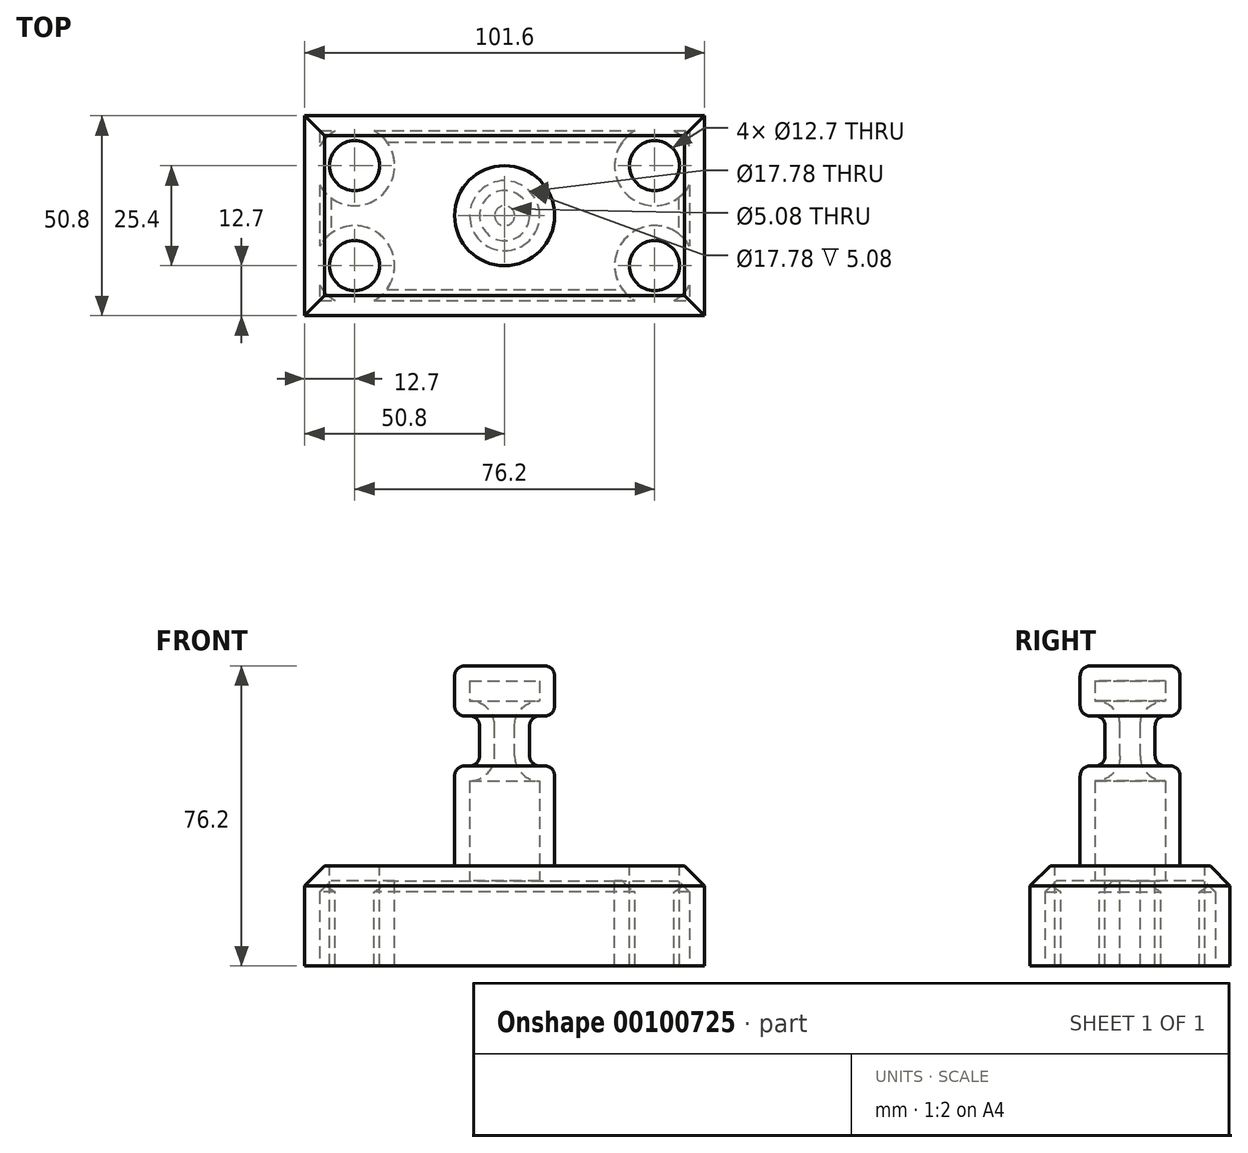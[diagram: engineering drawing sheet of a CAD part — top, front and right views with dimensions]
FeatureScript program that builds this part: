
annotation { "Feature Type Name" : "Feature", "Feature Type Description" : "" }
export const myFeature = defineFeature(function(context is Context, id is Id, definition is map)
    precondition{}
    {
        {
            var Q0;
            Q0=qCreatedBy(makeId("Top.planeOp"),FACE);
            var sketch = newSketch(context, id + "F0", { "sketchPlane" : qUnion([Q0])});
            skLineSegment(sketch, "E0.bottom", {"start": v(-50.8, 25.4) * mm, "end": v(50.8, 25.4) * mm});
            skLineSegment(sketch, "E0.top", {"start": v(-50.8, -25.4) * mm, "end": v(50.8, -25.4) * mm});
            skLineSegment(sketch, "E0.left", {"start": v(-50.8, 25.4) * mm, "end": v(-50.8, -25.4) * mm});
            skLineSegment(sketch, "E0.right", {"start": v(50.8, 25.4) * mm, "end": v(50.8, -25.4) * mm});
            skPoint(sketch, "E0.middle", {"position": v(0, 0) * mm});
            skSolve(sketch);
        }
        {
            var Q0;
            Q0=makeQuery(id+"F0.imprint","IMPRINT",FACE,{"disambiguationData":[TD([[makeQuery(id+"F0.imprint","IMPRINT",EDGE,{"derivedFrom":sQuery(id+"F0.wireOp",EDGE,"E0.bottom")}),-1.0]])]});
            extrude(context, id + "F1", {"entities" : qUnion([Q0]), "depth" : 25.4 * mm});
        }
        {
            var Q0;
            Q0=makeQuery(id+"F1.opExtrude","CAP_FACE",FACE,{"disambiguationData":[OSD([sQuery(id+"F0.wireOp",EDGE,"E0.bottom"),sQuery(id+"F0.wireOp",EDGE,"E0.top"),sQuery(id+"F0.wireOp",EDGE,"E0.left"),sQuery(id+"F0.wireOp",EDGE,"E0.right")])],"isStart":false});
            var sketch = newSketch(context, id + "F2", { "sketchPlane" : qUnion([Q0])});
            skCircle(sketch, "E1", {"center": v(-38.1, 12.7) * mm, "radius": 6.35 * mm});
            skCircle(sketch, "E2", {"center": v(38.1, 12.7) * mm, "radius": 6.35 * mm});
            skCircle(sketch, "E3", {"center": v(38.1, -12.7) * mm, "radius": 6.35 * mm});
            skCircle(sketch, "E4", {"center": v(-38.1, -12.7) * mm, "radius": 6.35 * mm});
            skSolve(sketch);
        }
        {
            var Q0;
            Q0 = qSketchRegion(id + "F2", true);
            extrude(context, id + "F3", {"entities" : qUnion([Q0]), "operationType" : NewBodyOperationType.REMOVE, "endBound" : BoundingType.THROUGH_ALL, "oppositeDirection" : true, "depth" : 25.4 * mm});
        }
        {
            var Q0;
            Q0=qCreatedBy(makeId("Front.planeOp"),FACE);
            var sketch = newSketch(context, id + "F4", { "sketchPlane" : qUnion([Q0])});
            skLineSegment(sketch, "E5.bottom", {"start": v(0, 25.4) * mm, "end": v(-12.7, 25.4) * mm});
            skLineSegment(sketch, "E5.top", {"start": v(0, 76.2) * mm, "end": v(-12.7, 76.2) * mm});
            skLineSegment(sketch, "E5.left", {"start": v(0, 25.4) * mm, "end": v(0, 76.2) * mm});
            skLineSegment(sketch, "E5.right", {"start": v(-12.7, 25.4) * mm, "end": v(-12.7, 76.2) * mm});
            skSolve(sketch);
        }
        {
            var Q0;
            Q0=makeQuery(id+"F4.imprint","IMPRINT",FACE,{"disambiguationData":[TD([[makeQuery(id+"F4.imprint","IMPRINT",EDGE,{"derivedFrom":sQuery(id+"F4.wireOp",EDGE,"E5.bottom")}),-1.0]])]});
            var Q1;
            Q1=sQuery(id+"F4.wireOp",EDGE,"E5.left");
            revolve(context, id + "F5", {"operationType" : NewBodyOperationType.ADD, "entities" : qUnion([Q0]), "axis" : qUnion([Q1]), "revolveType" : RevolveType.FULL});
        }
        {
            var Q0;
            Q0=qCreatedBy(makeId("Front.planeOp"),FACE);
            var sketch = newSketch(context, id + "F6", { "sketchPlane" : qUnion([Q0])});
            skLineSegment(sketch, "E6.bottom", {"start": v(-16.07, 63.5) * mm, "end": v(-6.35, 63.5) * mm});
            skLineSegment(sketch, "E6.top", {"start": v(-16.07, 50.8) * mm, "end": v(-6.35, 50.8) * mm});
            skLineSegment(sketch, "E6.left", {"start": v(-16.07, 63.5) * mm, "end": v(-16.07, 50.8) * mm});
            skLineSegment(sketch, "E6.right", {"start": v(-6.35, 63.5) * mm, "end": v(-6.35, 50.8) * mm});
            skLineSegment(sketch, "E7", {"start": v(0, 0) * mm, "end": v(0, 76.26) * mm, "construction": true});
            skSolve(sketch);
        }
        {
            var Q0;
            Q0=makeQuery(id+"F6.imprint","IMPRINT",FACE,{"disambiguationData":[TD([[makeQuery(id+"F6.imprint","IMPRINT",EDGE,{"derivedFrom":sQuery(id+"F6.wireOp",EDGE,"E6.bottom")}),-1.0]])]});
            var Q1;
            Q1=sQuery(id+"F6.wireOp",EDGE,"E7");
            revolve(context, id + "F7", {"operationType" : NewBodyOperationType.REMOVE, "entities" : qUnion([Q0]), "axis" : qUnion([Q1]), "revolveType" : RevolveType.FULL, "oppositeDirection" : true});
        }
        {
            var Q0;
            Q0=makeQuery(id+"F7.boolean.opBoolean","INTERSECT",EDGE,{"derivedFrom":[makeQuery(id+"F5.opRevolve","SWEPT_FACE",FACE,{"disambiguationData":[OSD([sQuery(id+"F4.wireOp",EDGE,"E5.right")])]}),makeQuery(id+"F7.opRevolve","SWEPT_FACE",FACE,{"disambiguationData":[OSD([sQuery(id+"F6.wireOp",EDGE,"E6.top")])]})]});
            var Q1;
            Q1=makeQuery(id+"F7.boolean.opBoolean","COPY",EDGE,{"derivedFrom":makeQuery(id+"F7.opRevolve","SWEPT_EDGE",EDGE,{"disambiguationData":[OSD([sQuery(id+"F6.wireOp",EDGE,"E6.top"),sQuery(id+"F6.wireOp",EDGE,"E6.right")])]})});
            var Q2;
            Q2=makeQuery(id+"F7.boolean.opBoolean","COPY",EDGE,{"derivedFrom":makeQuery(id+"F7.opRevolve","SWEPT_EDGE",EDGE,{"disambiguationData":[OSD([sQuery(id+"F6.wireOp",EDGE,"E6.bottom"),sQuery(id+"F6.wireOp",EDGE,"E6.right")])]})});
            var Q3;
            Q3=makeQuery(id+"F7.boolean.opBoolean","INTERSECT",EDGE,{"derivedFrom":[makeQuery(id+"F5.opRevolve","SWEPT_FACE",FACE,{"disambiguationData":[OSD([sQuery(id+"F4.wireOp",EDGE,"E5.right")])]}),makeQuery(id+"F7.opRevolve","SWEPT_FACE",FACE,{"disambiguationData":[OSD([sQuery(id+"F6.wireOp",EDGE,"E6.bottom")])]})]});
            var Q4;
            Q4=makeQuery(id+"F5.opRevolve","SWEPT_EDGE",EDGE,{"disambiguationData":[OSD([sQuery(id+"F4.wireOp",EDGE,"E5.top"),sQuery(id+"F4.wireOp",EDGE,"E5.right")])]});
            fillet(context, id + "F8", {"entities" : qUnion([Q0, Q1, Q2, Q3, Q4]), "radius" : 2.54 * mm, "tangentPropagation" : true, "allowEdgeOverflow" : false});
        }
        {
            var Q0;
            Q0=makeQuery(id+"F1.opExtrude","CAP_EDGE",EDGE,{"disambiguationData":[OSD([sQuery(id+"F0.wireOp",EDGE,"E0.top")])],"isStart":false});
            var Q1;
            Q1=makeQuery(id+"F1.opExtrude","CAP_EDGE",EDGE,{"disambiguationData":[OSD([sQuery(id+"F0.wireOp",EDGE,"E0.left")])],"isStart":false});
            var Q2;
            Q2=makeQuery(id+"F1.opExtrude","CAP_EDGE",EDGE,{"disambiguationData":[OSD([sQuery(id+"F0.wireOp",EDGE,"E0.right")])],"isStart":false});
            var Q3;
            Q3=makeQuery(id+"F1.opExtrude","CAP_EDGE",EDGE,{"disambiguationData":[OSD([sQuery(id+"F0.wireOp",EDGE,"E0.bottom")])],"isStart":false});
            chamfer(context, id + "F9", {"entities" : qUnion([Q0, Q1, Q2, Q3]), "width" : 5.08 * mm, "tangentPropagation" : true});
        }
        {
            var Q0;
            Q0=makeQuery(id+"F1.opExtrude","CAP_FACE",FACE,{"disambiguationData":[OSD([sQuery(id+"F0.wireOp",EDGE,"E0.bottom"),sQuery(id+"F0.wireOp",EDGE,"E0.top"),sQuery(id+"F0.wireOp",EDGE,"E0.left"),sQuery(id+"F0.wireOp",EDGE,"E0.right")])],"isStart":true});
            shell(context, id + "F10", {"entities" : qUnion([Q0]), "thickness" : 3.8 * mm});
        }
    });
